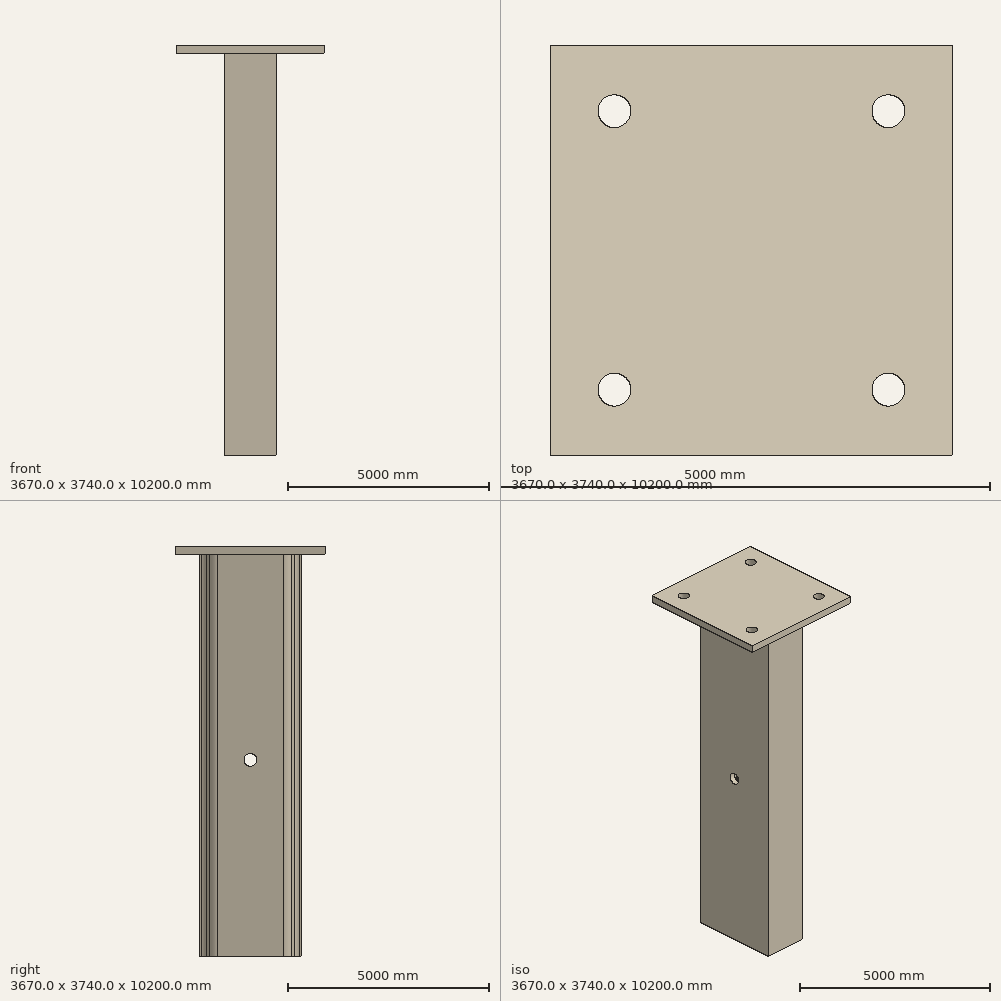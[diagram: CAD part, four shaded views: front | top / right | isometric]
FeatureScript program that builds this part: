
annotation { "Feature Type Name" : "Feature", "Feature Type Description" : "" }
export const myFeature = defineFeature(function(context is Context, id is Id, definition is map)
    precondition{}
    {
        {
            var Q0;
            Q0=qCreatedBy(makeId("Top.planeOp"),FACE);
            var sketch = newSketch(context, id + "F0", { "sketchPlane" : qUnion([Q0])});
            skLineSegment(sketch, "E0", {"start": v(-635, -1270) * mm, "end": v(-635, 1270) * mm});
            skLineSegment(sketch, "E1", {"start": v(-635, 1270) * mm, "end": v(635, 1270) * mm});
            skLineSegment(sketch, "E2", {"start": v(635, 1270) * mm, "end": v(635, 1210.42) * mm});
            skArc(sketch, "E3", {"start": v(529.81, 1096.49) * mm, "mid": v(604.68, 1132.89) * mm, "end": v(635, 1210.42) * mm});
            skLineSegment(sketch, "E4", {"start": v(529.81, 1096.49) * mm, "end": v(-283.92, 1031.39) * mm});
            skArc(sketch, "E5", {"start": v(-283.92, 1031.39) * mm, "mid": v(-425.33, 962.62) * mm, "end": v(-482.6, 816.17) * mm});
            skLineSegment(sketch, "E6", {"start": v(-482.6, 816.17) * mm, "end": v(-482.6, -816.17) * mm});
            skArc(sketch, "E7", {"start": v(-482.6, -816.17) * mm, "mid": v(-425.33, -962.62) * mm, "end": v(-283.92, -1031.39) * mm});
            skLineSegment(sketch, "E8", {"start": v(-283.92, -1031.39) * mm, "end": v(529.81, -1096.49) * mm});
            skArc(sketch, "E9", {"start": v(635, -1210.42) * mm, "mid": v(604.68, -1132.89) * mm, "end": v(529.81, -1096.49) * mm});
            skLineSegment(sketch, "E10", {"start": v(635, -1210.42) * mm, "end": v(635, -1270) * mm});
            skLineSegment(sketch, "E11", {"start": v(635, -1270) * mm, "end": v(-635, -1270) * mm});
            skSolve(sketch);
        }
        {
            var Q0;
            Q0 = qSketchRegion(id + "F0", true);
            extrude(context, id + "F1", {"entities" : qUnion([Q0]), "depth" : 10000 * mm});
        }
        {
            var Q0;
            Q0=makeQuery(id+"F1.opExtrude","CAP_FACE",FACE,{"disambiguationData":[OSD([sQuery(id+"F0.wireOp",EDGE,"E0"),sQuery(id+"F0.wireOp",EDGE,"E1"),sQuery(id+"F0.wireOp",EDGE,"E2"),sQuery(id+"F0.wireOp",EDGE,"E3"),sQuery(id+"F0.wireOp",EDGE,"E4"),sQuery(id+"F0.wireOp",EDGE,"E5"),sQuery(id+"F0.wireOp",EDGE,"E6"),sQuery(id+"F0.wireOp",EDGE,"E7"),sQuery(id+"F0.wireOp",EDGE,"E8"),sQuery(id+"F0.wireOp",EDGE,"E9"),sQuery(id+"F0.wireOp",EDGE,"E10"),sQuery(id+"F0.wireOp",EDGE,"E11")])],"isStart":false});
            var sketch = newSketch(context, id + "F2", { "sketchPlane" : qUnion([Q0])});
            skLineSegment(sketch, "E12.bottom", {"start": v(1835, -1870) * mm, "end": v(-1835, -1870) * mm});
            skLineSegment(sketch, "E12.top", {"start": v(1835, 1870) * mm, "end": v(-1835, 1870) * mm});
            skLineSegment(sketch, "E12.left", {"start": v(1835, -1870) * mm, "end": v(1835, 1870) * mm});
            skLineSegment(sketch, "E12.right", {"start": v(-1835, -1870) * mm, "end": v(-1835, 1870) * mm});
            skCircle(sketch, "E13", {"center": v(-1249.3, -1270) * mm, "radius": 150 * mm});
            skCircle(sketch, "E14.MirrorC", {"center": v(-1249.3, 1270) * mm, "radius": 150 * mm});
            skCircle(sketch, "E15.MirrorC", {"center": v(1249.3, 1270) * mm, "radius": 150 * mm});
            skCircle(sketch, "E16.MirrorC", {"center": v(1249.3, -1270) * mm, "radius": 150 * mm});
            skSolve(sketch);
        }
        {
            var Q0;
            Q0 = qSketchRegion(id + "F2", true);
            extrude(context, id + "F3", {"entities" : qUnion([Q0]), "operationType" : NewBodyOperationType.ADD, "depth" : 200 * mm});
        }
        {
            var Q0;
            Q0=makeQuery(id+"F1.opExtrude","SWEPT_FACE",FACE,{"disambiguationData":[OSD([sQuery(id+"F0.wireOp",EDGE,"E0")])]});
            var sketch = newSketch(context, id + "F4", { "sketchPlane" : qUnion([Q0])});
            skCircle(sketch, "E17", {"center": v(0, 4891.53) * mm, "radius": 158.18 * mm});
            skSolve(sketch);
        }
        {
            var Q0;
            Q0 = qSketchRegion(id + "F4", true);
            extrude(context, id + "F5", {"entities" : qUnion([Q0]), "operationType" : NewBodyOperationType.REMOVE, "endBound" : BoundingType.THROUGH_ALL, "oppositeDirection" : true, "depth" : 25 * mm});
        }
    });
